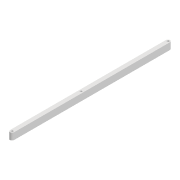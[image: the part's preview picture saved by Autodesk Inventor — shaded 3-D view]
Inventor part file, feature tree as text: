
AUTODESK INVENTOR PART (.ipt)
format: ipt  version: 2022 (Build 260153000, 153)  size: 93,696 bytes
history: native  units: mm
features: extrude x1, sketch x1
ambient origin geometry x8: Origin, YZ Plane, XZ Plane, XY Plane, X Axis, Y Axis, Z Axis, Center Point
bodies: Solid1 (feature_tree)
feature tree (2):
  extrude  "Extrusion1"  Depth=233.234mm
  sketch  "Sketch1"  dims[d0=6.0mm d1=233.234mm d2=3.0mm d3=3.0mm d4=10.0mm d5=0.0mm d16=3.0mm d17=103.234mm]
